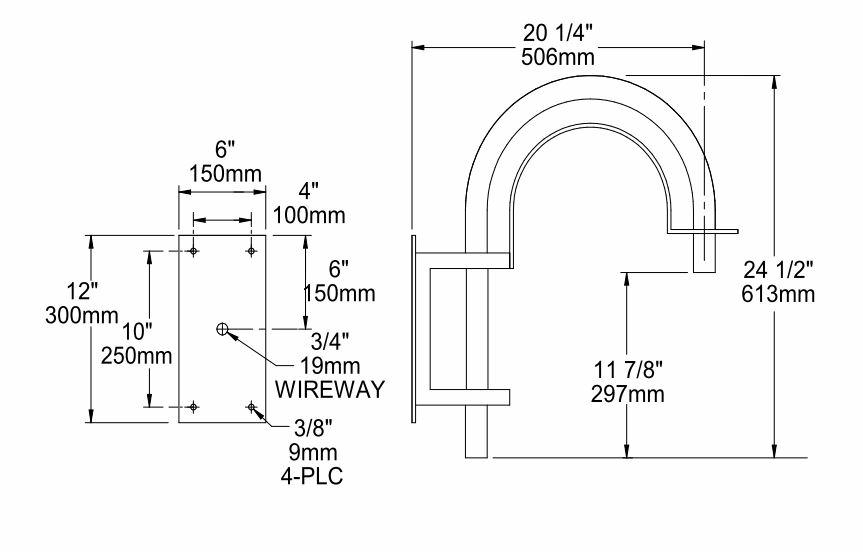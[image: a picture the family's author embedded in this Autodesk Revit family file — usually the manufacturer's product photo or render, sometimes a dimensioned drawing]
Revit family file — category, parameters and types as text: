
# Revit family: UCM
name_source: partatom
category: Lighting Fixtures
revit_build: Autodesk Revit MEP 2012 (Build: 20110309_2315(x64)
units: mm (PartAtom-declared; Revit-internal decimal feet)

## types (13) — shared parameters
Apparent Load = 70 VA
Architectural Design Manual = http://cdn.aal.net
Assembly Code = D5020200
Description = Lighting Fixture
Glass Material = Glass-AAL-Acrylic
Manufacturer = Architectural Area Lighting
MasterFormat Title = Area Lighting
Model = UCM
OmniClass Number = 23.80.70.14.11.14
OmniClass Title = Post-Top Lighting
Power Factor = 1
Type Comments = on relamp door. full cutoff
URL = www.aal.net
Voltage = 120 V
Wattage = 79 W
Wattage Comments = 49W to 79W
zero-valued in all types: Default elevation

## per-type parameters (varying)
| type | Housing Material |
| UCM - AWT | Aluminum-AAL-Artic White |
| UCM - BLK | Aluminum-AAL-Weathered Bronze |
| UCM - MTB | Aluminum-AAL-Matte Black |
| UCM - DGN | Aluminum-AAL-Dark Green |
| UCM - DBZ | Aluminum-AAL-Dark Bronze |
| UCM - WRZ | Aluminum-AAL-Weathered Bronze |
| UCM - BRM | Aluminum-AAL-Metalic Bronze |
| UCM - VBL | Aluminum-AAL-Verde Blue |
| UCM - CRT | Aluminum-AAL-Corten |
| UCM - MAL | Aluminum-AAL-Matte |
| UCM - MDG | Aluminum-AAL-Medium Grey |
| UCM - ATG | Aluminum-AAL-Antique Green |
| UCM - LGY | Aluminum-AAL-Light Grey |

## geometry (parser evidence)
native form markers: Blend x22, Sweep x36
no freeform markers — native parametric forms only
